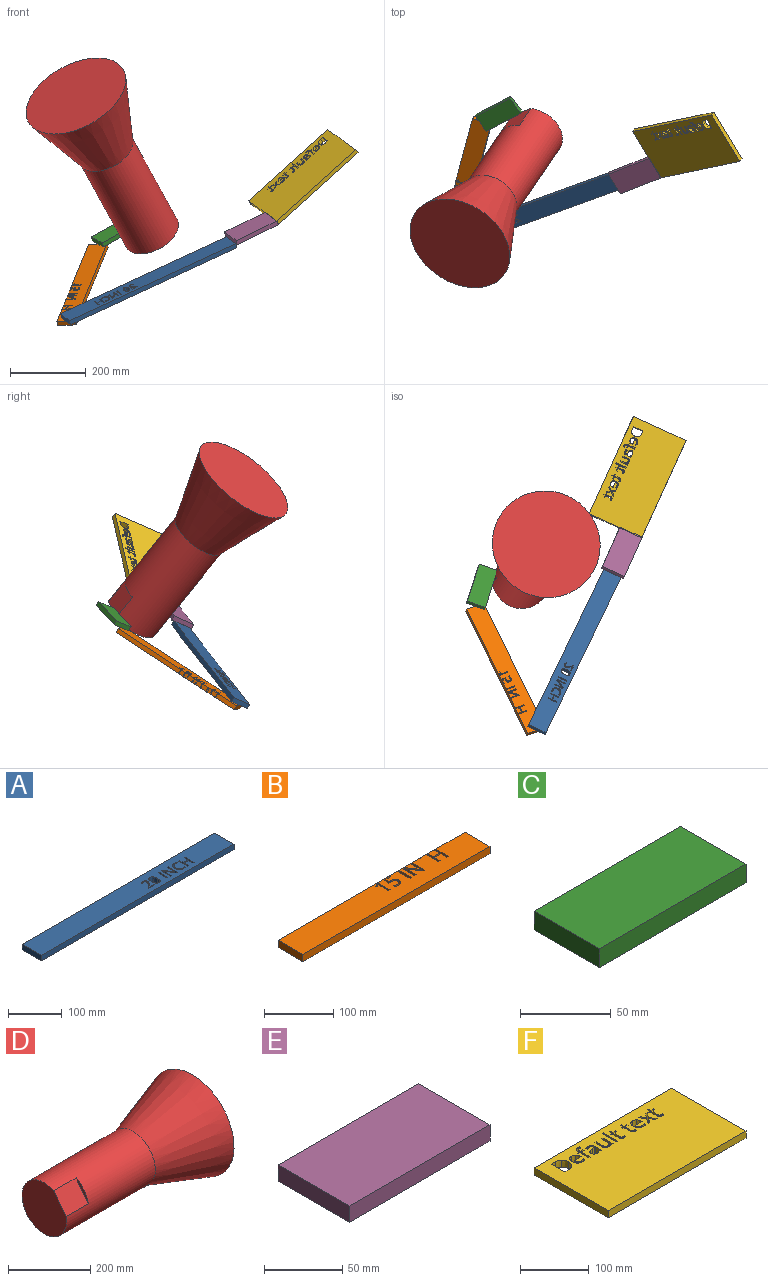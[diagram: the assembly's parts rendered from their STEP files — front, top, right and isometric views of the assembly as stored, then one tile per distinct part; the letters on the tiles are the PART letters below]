
ASSEMBLY  parts=6 mates=5
PART A: 80 faces, bbox 508x50.8x12.7 mm
  f0: plane 12.7x2.44mm, normal (-1,0,0), area 31mm2, adj f1,f77,f78,f79
  f1: plane 15.23x12.7mm, normal (0,1,0), area 193.5mm2, adj f0,f2,f78,f79
  f2: plane 12.7x2.27mm, normal (1,0,0), area 28.8mm2, adj f1,f3,f78,f79
  f3: plane 12.7x6.13mm, normal (0.71,-0.71,0), area 109.9mm2, adj f2,f4,f78,f79
  f4: extruded ~12.7x4.03mm, area 69.3mm2, adj f3,f5,f78,f79
  f5: extruded ~12.7x2.35mm, area 34.4mm2, adj f4,f6,f78,f79
  f6: extruded ~12.7x2.46mm, area 31.9mm2, adj f5,f7,f78,f79
  f7: extruded ~12.7x2.94mm, area 41.2mm2, adj f6,f8,f78,f79
  f8: extruded ~12.7x3.13mm, area 43.1mm2, adj f7,f9,f78,f79
  f9: extruded ~12.7x2.73mm, area 35.4mm2, adj f8,f10,f78,f79
  f10: extruded ~12.7x2.88mm, area 42.8mm2, adj f9,f11,f78,f79
  f11: plane 12.7x1.79mm, normal (0.79,0.61,0), area 28.8mm2, adj f10,f12,f78,f79
  f12: extruded ~12.7x6.98mm, area 96.8mm2, adj f11,f13,f78,f79
  f13: extruded ~12.7x5.12mm, area 70mm2, adj f12,f14,f78,f79
  f14: extruded ~12.7x4.49mm, area 63.7mm2, adj f13,f15,f78,f79
  f15: extruded ~12.7x4.36mm, area 58.3mm2, adj f14,f16,f78,f79
  f16: extruded ~12.7x5.45mm, area 91.1mm2, adj f15,f17,f78,f79
  f17: plane 12.7x5.07mm, normal (-0.7,0.71,0), area 90.1mm2, adj f16,f18,f78,f79
  f18: plane 12.7x0.13mm, normal (-1,0,0), area 1.6mm2, adj f17,f77,f78,f79
  f19: extruded ~12.7x8.86mm, area 116.7mm2, adj f20,f71,f78,f79
  f20: extruded ~12.7x8.98mm, area 118mm2, adj f19,f21,f78,f79
  f21: extruded ~12.7x5.8mm, area 86.6mm2, adj f20,f22,f78,f79
  f22: extruded ~12.7x5.69mm, area 85.8mm2, adj f21,f23,f78,f79
  f23: extruded ~12.7x8.91mm, area 117.3mm2, adj f22,f24,f78,f79
  f24: extruded ~12.7x8.99mm, area 118.1mm2, adj f23,f25,f78,f79
  f25: extruded ~12.7x5.75mm, area 85.9mm2, adj f24,f71,f78,f79
  f26: plane 23.18x12.7mm, normal (-1,0,0), area 294.4mm2, adj f27,f72,f78,f79
  f27: plane 12.7x2.69mm, normal (0,1,0), area 34.2mm2, adj f26,f28,f78,f79
  f28: plane 12.7x10.91mm, normal (1,0,0), area 138.5mm2, adj f27,f29,f78,f79
  f29: plane 12.7x12.21mm, normal (0,1,0), area 155.1mm2, adj f28,f30,f78,f79
  f30: plane 12.7x10.91mm, normal (-1,0,0), area 138.5mm2, adj f29,f31,f78,f79
  f31: plane 12.7x2.69mm, normal (0,1,0), area 34.2mm2, adj f30,f32,f78,f79
  f32: plane 23.18x12.7mm, normal (1,0,0), area 294.4mm2, adj f31,f33,f78,f79
  f33: plane 12.7x2.69mm, normal (0,-1,0), area 34.2mm2, adj f32,f34,f78,f79
  f34: plane 12.7x9.86mm, normal (-1,0,0), area 125.2mm2, adj f33,f35,f78,f79
  f35: plane 12.7x12.21mm, normal (0,-1,0), area 155.1mm2, adj f34,f36,f78,f79
  f36: plane 12.7x9.86mm, normal (1,0,0), area 125.2mm2, adj f35,f72,f78,f79
  f37: extruded ~12.7x5.27mm, area 69.2mm2, adj f38,f73,f78,f79
  f38: extruded ~12.7x6.03mm, area 85.9mm2, adj f37,f39,f78,f79
  f39: extruded ~12.7x6.97mm, area 94.9mm2, adj f38,f40,f78,f79
  f40: extruded ~12.7x7.03mm, area 95.3mm2, adj f39,f41,f78,f79
  f41: extruded ~12.7x6.08mm, area 86.2mm2, adj f40,f42,f78,f79
  f42: extruded ~12.7x5.53mm, area 71.4mm2, adj f41,f43,f78,f79
  f43: plane 12.7x2.36mm, normal (-1,0,0), area 30mm2, adj f42,f44,f78,f79
  f44: extruded ~12.7x5.95mm, area 76.8mm2, adj f43,f45,f78,f79
  f45: extruded ~12.7x7.9mm, area 111.3mm2, adj f44,f46,f78,f79
  f46: extruded ~12.7x8.83mm, area 120.3mm2, adj f45,f47,f78,f79
  f47: extruded ~12.7x6.28mm, area 82.2mm2, adj f46,f48,f78,f79
  f48: extruded ~12.7x4.15mm, area 73.1mm2, adj f47,f49,f78,f79
  f49: extruded ~12.7x5.95mm, area 78.7mm2, adj f48,f50,f78,f79
  f50: extruded ~12.7x6.37mm, area 83.4mm2, adj f49,f73,f78,f79
  f51: plane 23.18x12.7mm, normal (-1,0,0), area 294.4mm2, adj f52,f74,f78,f79
  f52: plane 12.7x3.07mm, normal (0,1,0), area 39mm2, adj f51,f53,f78,f79
  f53: plane 19.45x12.7mm, normal (0.84,0.55,0), area 294.8mm2, adj f52,f54,f78,f79
  f54: plane 12.7x0.13mm, normal (0,1,0), area 1.6mm2, adj f53,f55,f78,f79
  f55: extruded ~12.7x6.28mm, area 79.8mm2, adj f54,f56,f78,f79
  f56: plane 13.17x12.7mm, normal (-1,0,0), area 167.3mm2, adj f55,f57,f78,f79
  f57: plane 12.7x2.49mm, normal (0,1,0), area 31.6mm2, adj f56,f58,f78,f79
  f58: plane 23.18x12.7mm, normal (1,0,0), area 294.4mm2, adj f57,f59,f78,f79
  f59: plane 12.7x3.04mm, normal (0,-1,0), area 38.7mm2, adj f58,f60,f78,f79
  f60: plane 19.37x12.7mm, normal (-0.84,-0.55,0), area 293.8mm2, adj f59,f61,f78,f79
  f61: plane 12.7x0.13mm, normal (0,-1,0), area 1.6mm2, adj f60,f62,f78,f79
  f62: extruded ~12.7x2.75mm, area 35mm2, adj f61,f63,f78,f79
  f63: extruded ~12.7x3.32mm, area 42.2mm2, adj f62,f64,f78,f79
  f64: plane 13.3x12.7mm, normal (1,0,0), area 168.9mm2, adj f63,f74,f78,f79
  f65: plane 12.7x2.69mm, normal (0,1,0), area 34.2mm2, adj f66,f75,f78,f79
  f66: plane 23.18x12.7mm, normal (1,0,0), area 294.4mm2, adj f65,f67,f78,f79
  f67: plane 12.7x2.69mm, normal (0,-1,0), area 34.2mm2, adj f66,f75,f78,f79
  f68: plane 50.8x12.7mm, normal (1,0,0), area 645.2mm2, adj f69,f76,f78,f79
  f69: plane 508x12.7mm, normal (0,1,0), area 6451.6mm2, adj f68,f70,f78,f79
  f70: plane 50.8x12.7mm, normal (-1,0,0), area 645.2mm2, adj f69,f76,f78,f79
  f71: extruded ~12.7x5.73mm, area 86.5mm2, adj f19,f25,f78,f79
  f72: plane 12.7x2.69mm, normal (0,-1,0), area 34.2mm2, adj f26,f36,f78,f79
  f73: plane 12.7x2.31mm, normal (-0.9,0.44,0), area 32.8mm2, adj f37,f50,f78,f79
  f74: plane 12.7x2.52mm, normal (0,-1,0), area 32mm2, adj f51,f64,f78,f79
  f75: plane 23.18x12.7mm, normal (-1,0,0), area 294.4mm2, adj f65,f67,f78,f79
  f76: plane 508x12.7mm, normal (0,-1,0), area 6451.6mm2, adj f68,f70,f78,f79
  f77: plane 12.7x11.92mm, normal (0,-1,0), area 151.4mm2, adj f0,f18,f78,f79
  f78: plane 508x50.8mm, normal (0,0,1), area 24872.1mm2, adj f0,f1,f2,f3,f4,f5,f6,f7
  f79: plane 508x50.8mm, normal (0,0,-1), area 24872.1mm2, adj f0,f1,f2,f3,f4,f5,f6,f7
PART B: 68 faces, bbox 381x50.9x12.7 mm
  f0: plane 25.19x12.7mm, normal (-1,0,0), area 319.8mm2, adj f1,f65,f66,f67
  f1: plane 12.7x2.79mm, normal (0,1,0), area 35.4mm2, adj f0,f2,f66,f67
  f2: plane 17.95x12.7mm, normal (1,0,0), area 227.9mm2, adj f1,f3,f66,f67
  f3: extruded ~12.7x4.24mm, area 53.9mm2, adj f2,f4,f66,f67
  f4: extruded ~12.7x0.81mm, area 14.1mm2, adj f3,f5,f66,f67
  f5: extruded ~12.7x4.1mm, area 67.3mm2, adj f4,f6,f66,f67
  f6: plane 12.7x1.96mm, normal (0.79,0.61,0), area 31.5mm2, adj f5,f7,f66,f67
  f7: plane 12.7x6.66mm, normal (0.61,-0.79,0), area 107mm2, adj f6,f65,f66,f67
  f8: extruded ~12.7x3.95mm, area 50.5mm2, adj f9,f60,f66,f67
  f9: extruded ~12.7x6.26mm, area 85.2mm2, adj f8,f10,f66,f67
  f10: extruded ~12.7x5.4mm, area 77mm2, adj f9,f11,f66,f67
  f11: extruded ~12.7x6.13mm, area 86.7mm2, adj f10,f12,f66,f67
  f12: extruded ~12.7x6.87mm, area 93.8mm2, adj f11,f13,f66,f67
  f13: extruded ~12.7x6.49mm, area 85.3mm2, adj f12,f14,f66,f67
  f14: plane 12.7x2.76mm, normal (1,0,0), area 35mm2, adj f13,f15,f66,f67
  f15: extruded ~12.7x2.99mm, area 41.2mm2, adj f14,f16,f66,f67
  f16: extruded ~12.7x3.53mm, area 45.3mm2, adj f15,f17,f66,f67
  f17: extruded ~12.7x4.71mm, area 63.8mm2, adj f16,f18,f66,f67
  f18: extruded ~12.7x4.14mm, area 58.6mm2, adj f17,f19,f66,f67
  f19: extruded ~12.7x6.45mm, area 121.1mm2, adj f18,f20,f66,f67
  f20: extruded ~12.7x4.38mm, area 56mm2, adj f19,f21,f66,f67
  f21: plane 12.7x1.48mm, normal (0.54,0.84,0), area 22.4mm2, adj f20,f22,f66,f67
  f22: plane 12.7x11.79mm, normal (1,-0.08,0), area 150.2mm2, adj f21,f23,f66,f67
  f23: plane 12.7x12.52mm, normal (0,-1,0), area 159mm2, adj f22,f24,f66,f67
  f24: plane 12.7x2.64mm, normal (-1,0,0), area 33.5mm2, adj f23,f25,f66,f67
  f25: plane 12.7x10.08mm, normal (0,1,0), area 128mm2, adj f24,f60,f66,f67
  f26: plane 12.7x2.93mm, normal (0,1,0), area 37.2mm2, adj f27,f61,f66,f67
  f27: plane 25.19x12.7mm, normal (1,0,0), area 319.8mm2, adj f26,f28,f66,f67
  f28: plane 12.7x2.93mm, normal (0,-1,0), area 37.2mm2, adj f27,f61,f66,f67
  f29: plane 25.19x12.7mm, normal (-1,0,0), area 319.8mm2, adj f30,f62,f66,f67
  f30: plane 12.7x3.34mm, normal (0,1,0), area 42.4mm2, adj f29,f31,f66,f67
  f31: plane 21.13x13.76mm, normal (0.84,0.55,0), area 320.3mm2, adj f30,f32,f66,f67
  f32: plane 12.7x0.14mm, normal (0,1,0), area 1.8mm2, adj f31,f33,f66,f67
  f33: extruded ~12.7x6.82mm, area 86.7mm2, adj f32,f34,f66,f67
  f34: plane 14.32x12.7mm, normal (-1,0,0), area 181.8mm2, adj f33,f35,f66,f67
  f35: plane 12.7x2.71mm, normal (0,1,0), area 34.4mm2, adj f34,f36,f66,f67
  f36: plane 25.19x12.7mm, normal (1,0,0), area 319.8mm2, adj f35,f37,f66,f67
  f37: plane 12.7x3.31mm, normal (0,-1,0), area 42mm2, adj f36,f38,f66,f67
  f38: plane 21.05x13.73mm, normal (-0.84,-0.55,0), area 319.2mm2, adj f37,f39,f66,f67
  f39: plane 12.7x0.14mm, normal (0,-1,0), area 1.8mm2, adj f38,f40,f66,f67
  f40: extruded ~12.7x2.99mm, area 38mm2, adj f39,f41,f66,f67
  f41: extruded ~12.7x3.61mm, area 45.9mm2, adj f40,f42,f66,f67
  f42: plane 14.45x12.7mm, normal (1,0,0), area 183.6mm2, adj f41,f62,f66,f67
  f43: plane 25.19x12.7mm, normal (-1,0,0), area 319.8mm2, adj f44,f63,f66,f67
  f44: plane 12.7x2.93mm, normal (0,1,0), area 37.2mm2, adj f43,f45,f66,f67
  f45: plane 12.7x11.85mm, normal (1,0,0), area 150.5mm2, adj f44,f46,f66,f67
  f46: plane 13.27x12.7mm, normal (0,1,0), area 168.5mm2, adj f45,f47,f66,f67
  f47: plane 12.7x11.85mm, normal (-1,0,0), area 150.5mm2, adj f46,f48,f66,f67
  f48: plane 12.7x2.93mm, normal (0,1,0), area 37.2mm2, adj f47,f49,f66,f67
  f49: plane 25.19x12.7mm, normal (1,0,0), area 319.8mm2, adj f48,f50,f66,f67
  f50: plane 12.7x2.93mm, normal (0,-1,0), area 37.2mm2, adj f49,f51,f66,f67
  f51: plane 12.7x10.72mm, normal (-1,0,0), area 136.1mm2, adj f50,f52,f66,f67
  f52: plane 13.27x12.7mm, normal (0,-1,0), area 168.5mm2, adj f51,f53,f66,f67
  f53: plane 12.7x10.72mm, normal (1,0,0), area 136.1mm2, adj f52,f63,f66,f67
  f54: extruded ~12.7x2.15mm, area 27.4mm2, adj f55,f64,f66,f67
  f55: plane 288.57x12.7mm, normal (0,1,0), area 3664.8mm2, adj f54,f56,f66,f67
  f56: plane 50.8x12.7mm, normal (-1,0,0), area 645.2mm2, adj f55,f57,f66,f67
  f57: plane 381x12.7mm, normal (0,-1,0), area 4838.7mm2, adj f56,f58,f66,f67
  f58: plane 50.8x12.7mm, normal (1,0,0), area 645.2mm2, adj f57,f59,f66,f67
  f59: plane 87.89x12.7mm, normal (0,1,0), area 1116.2mm2, adj f58,f64,f66,f67
  f60: plane 12.7x7.56mm, normal (-1,0.08,0), area 96.4mm2, adj f8,f25,f66,f67
  f61: plane 25.19x12.7mm, normal (-1,0,0), area 319.8mm2, adj f26,f28,f66,f67
  f62: plane 12.7x2.74mm, normal (0,-1,0), area 34.8mm2, adj f29,f42,f66,f67
  f63: plane 12.7x2.93mm, normal (0,-1,0), area 37.2mm2, adj f43,f53,f66,f67
  f64: extruded ~12.7x2.4mm, area 30.5mm2, adj f54,f59,f66,f67
  f65: plane 12.7x2.41mm, normal (0,-1,0), area 30.6mm2, adj f0,f7,f66,f67
  f66: plane 381x50.94mm, normal (0,0,1), area 18655.9mm2, adj f0,f1,f2,f3,f4,f5,f6,f7
  f67: plane 381x50.94mm, normal (0,0,-1), area 18655.9mm2, adj f0,f1,f2,f3,f4,f5,f6,f7
PART C: 6 faces, bbox 114.3x50.8x12.7 mm
  f0: plane 50.8x12.7mm, normal (1,0,0), area 645.2mm2, adj f1,f3,f4,f5
  f1: plane 114.3x12.7mm, normal (0,1,0), area 1451.6mm2, adj f0,f2,f4,f5
  f2: plane 50.8x12.7mm, normal (-1,0,0), area 645.2mm2, adj f1,f3,f4,f5
  f3: plane 114.3x12.7mm, normal (0,-1,0), area 1451.6mm2, adj f0,f2,f4,f5
  f4: plane 114.3x50.8mm, normal (0,0,1), area 5806.4mm2, adj f0,f1,f2,f3
  f5: plane 114.3x50.8mm, normal (0,0,-1), area 5806.4mm2, adj f0,f1,f2,f3
PART D: 6 faces, bbox 508x286.1x286.1 mm
  f0: cylinder r=76.2mm len=304.8mm, axis (-1,0,0), area 140438.7mm2, adj f1,f3,f4,f5
  f1: plane 152.4x152.4mm, normal (-1,0,0), area 17849.7mm2, adj f0,f4
  f2: plane 286.07x286.07mm, normal (1,0,0), area 64273.6mm2, adj f3
  f3: cone r=76.2mm half-angle=18.2deg, axis (1,0,0), area 147329.1mm2, adj f0,f2
  f4: plane 76.2x55.25mm, normal (0,-0.8,0.61), area 5290.5mm2, adj f0,f1,f5
  f5: plane 55.25x42.05mm, normal (-1,0,0), area 391.7mm2, adj f0,f4
PART E: 6 faces, bbox 127x64.3x12.7 mm
  f0: plane 127x12.7mm, normal (0,-1,0), area 1612.9mm2, adj f1,f3,f4,f5
  f1: plane 64.28x12.7mm, normal (1,0,0), area 816.4mm2, adj f0,f2,f4,f5
  f2: plane 127x12.7mm, normal (0,1,0), area 1612.9mm2, adj f1,f3,f4,f5
  f3: plane 64.28x12.7mm, normal (-1,0,0), area 816.4mm2, adj f0,f2,f4,f5
  f4: plane 127x64.28mm, normal (0,0,1), area 8164.1mm2, adj f0,f1,f2,f3
  f5: plane 127x64.28mm, normal (0,0,-1), area 8164.1mm2, adj f0,f1,f2,f3
PART F: 167 faces, bbox 284.2x152.4x12.7 mm
  f0: plane 284.16x152.4mm, normal (0,0,1), area 41292.7mm2, adj f2,f3,f4,f5,f6,f7,f8,f9
  f1: plane 284.16x152.4mm, normal (0,0,-1), area 41292.7mm2, adj f2,f3,f4,f5,f6,f7,f8,f9
  f2: plane 284.16x12.7mm, normal (0,-1,0), area 3608.9mm2, adj f0,f1,f3,f5
  f3: plane 152.4x12.7mm, normal (1,0,0), area 1935.5mm2, adj f0,f1,f2,f4
  f4: plane 284.16x12.7mm, normal (0,1,0), area 3608.9mm2, adj f0,f1,f3,f5
  f5: plane 152.4x12.7mm, normal (-1,0,0), area 1935.5mm2, adj f0,f1,f2,f4
  f6: plane 12.7x5.21mm, normal (0,1,0), area 66.1mm2, adj f0,f1,f7,f22
  f7: plane 12.7x2.41mm, normal (-1,0,0), area 30.6mm2, adj f0,f1,f6,f8
  f8: plane 12.7x5.21mm, normal (0,-1,0), area 66.1mm2, adj f0,f1,f7,f9
  f9: plane 12.7x1.33mm, normal (-1,0,0), area 16.8mm2, adj f0,f1,f8,f10
  f10: extruded ~12.7x3.74mm, area 49.4mm2, adj f0,f1,f9,f11
  f11: extruded ~12.7x2.59mm, area 37.6mm2, adj f0,f1,f10,f12
  f12: extruded ~12.7x3.06mm, area 39.7mm2, adj f0,f1,f11,f13
  f13: plane 12.7x2.48mm, normal (-0.95,0.31,0), area 33.2mm2, adj f0,f1,f12,f14
  f14: extruded ~12.7x3.81mm, area 49.2mm2, adj f0,f1,f13,f15
  f15: extruded ~12.7x7.54mm, area 145.7mm2, adj f0,f1,f14,f16
  f16: plane 12.7x1.13mm, normal (1,0,0), area 14.4mm2, adj f0,f1,f15,f17
  f17: plane 12.7x3.65mm, normal (0.29,-0.96,0), area 48.5mm2, adj f0,f1,f16,f18
  f18: plane 12.7x1.4mm, normal (1,0,0), area 17.7mm2, adj f0,f1,f17,f19
  f19: plane 12.7x3.65mm, normal (0,1,0), area 46.4mm2, adj f0,f1,f18,f20
  f20: plane 18.04x12.7mm, normal (1,0,0), area 229.1mm2, adj f0,f1,f19,f21
  f21: plane 12.7x3.1mm, normal (0,1,0), area 39.3mm2, adj f0,f1,f20,f22
  f22: plane 18.04x12.7mm, normal (-1,0,0), area 229.1mm2, adj f0,f1,f6,f21
  f23: extruded ~12.7x7.15mm, area 100.3mm2, adj f0,f1,f24,f36
  f24: extruded ~12.7x3.53mm, area 45.1mm2, adj f0,f1,f23,f25
  f25: extruded ~12.7x3.1mm, area 41.5mm2, adj f0,f1,f24,f26
  f26: plane 12.7x2.76mm, normal (-1,0,0), area 35.1mm2, adj f0,f1,f25,f27
  f27: extruded ~12.7x6.52mm, area 85.3mm2, adj f0,f1,f26,f28
  f28: extruded ~12.7x4.86mm, area 68.1mm2, adj f0,f1,f27,f29
  f29: extruded ~12.7x5.47mm, area 74.8mm2, adj f0,f1,f28,f30
  f30: plane 14.08x12.7mm, normal (0,1,0), area 178.8mm2, adj f0,f1,f29,f31
  f31: plane 12.7x1.96mm, normal (-1,0,0), area 24.9mm2, adj f0,f1,f30,f32
  f32: extruded ~12.7x6.67mm, area 91.4mm2, adj f0,f1,f31,f33
  f33: extruded ~12.7x6.08mm, area 86.3mm2, adj f0,f1,f32,f34
  f34: extruded ~12.7x6.54mm, area 94.1mm2, adj f0,f1,f33,f35
  f35: extruded ~12.7x7.86mm, area 106.7mm2, adj f0,f1,f34,f36
  f36: extruded ~12.7x7.67mm, area 105.5mm2, adj f0,f1,f23,f35
  f37: plane 12.7x2.91mm, normal (0.98,0.21,0), area 37.8mm2, adj f0,f1,f38,f55
  f38: plane 12.7x2.3mm, normal (0,1,0), area 29.2mm2, adj f0,f1,f37,f39
  f39: plane 13.96x12.7mm, normal (-1,0,0), area 177.3mm2, adj f0,f1,f38,f40
  f40: extruded ~12.7x5.2mm, area 71.8mm2, adj f0,f1,f39,f41
  f41: extruded ~12.7x5.42mm, area 73.5mm2, adj f0,f1,f40,f42
  f42: extruded ~12.7x3.61mm, area 46.4mm2, adj f0,f1,f41,f43
  f43: extruded ~12.7x3.31mm, area 45.2mm2, adj f0,f1,f42,f44
  f44: plane 12.7x2.37mm, normal (0.93,0.37,0), area 32.5mm2, adj f0,f1,f43,f45
  f45: extruded ~12.7x5.78mm, area 76.7mm2, adj f0,f1,f44,f46
  f46: extruded ~12.7x3.31mm, area 45.9mm2, adj f0,f1,f45,f47
  f47: extruded ~12.7x3.55mm, area 48mm2, adj f0,f1,f46,f48
  f48: plane 12.7x1.27mm, normal (1,0,0), area 16.1mm2, adj f0,f1,f47,f49
  f49: plane 12.7x3.47mm, normal (0.03,-1,0), area 44.1mm2, adj f0,f1,f48,f50
  f50: extruded ~12.7x9.9mm, area 169mm2, adj f0,f1,f49,f51
  f51: extruded ~12.7x4.46mm, area 62.6mm2, adj f0,f1,f50,f52
  f52: extruded ~12.7x4.76mm, area 65.2mm2, adj f0,f1,f51,f53
  f53: extruded ~12.7x3.8mm, area 49.4mm2, adj f0,f1,f52,f54
  f54: extruded ~12.7x3.05mm, area 51.4mm2, adj f0,f1,f53,f55
  f55: plane 12.7x0.15mm, normal (0,1,0), area 1.9mm2, adj f0,f1,f37,f54
  f56: plane 13.26x12.7mm, normal (-1,0,0), area 168.5mm2, adj f0,f1,f57,f72
  f57: plane 12.7x3.13mm, normal (0,-1,0), area 39.8mm2, adj f0,f1,f56,f58
  f58: plane 13.38x12.7mm, normal (1,0,0), area 169.9mm2, adj f0,f1,f57,f59
  f59: extruded ~12.7x5.67mm, area 77.9mm2, adj f0,f1,f58,f60
  f60: extruded ~12.7x5.58mm, area 76.3mm2, adj f0,f1,f59,f61
  f61: extruded ~12.7x3.86mm, area 50.4mm2, adj f0,f1,f60,f62
  f62: extruded ~12.7x2.64mm, area 45.2mm2, adj f0,f1,f61,f63
  f63: plane 12.7x0.17mm, normal (0,1,0), area 2.1mm2, adj f0,f1,f62,f64
  f64: plane 12.7x2.74mm, normal (0.99,0.16,0), area 35.3mm2, adj f0,f1,f63,f65
  f65: plane 12.7x2.56mm, normal (0,1,0), area 32.4mm2, adj f0,f1,f64,f66
  f66: plane 20.45x12.7mm, normal (-1,0,0), area 259.7mm2, adj f0,f1,f65,f67
  f67: plane 12.7x3.1mm, normal (0,-1,0), area 39.3mm2, adj f0,f1,f66,f68
  f68: plane 12.7x10.75mm, normal (1,0,0), area 136.5mm2, adj f0,f1,f67,f69
  f69: extruded ~12.7x5.73mm, area 76.6mm2, adj f0,f1,f68,f70
  f70: extruded ~12.7x4.69mm, area 65.7mm2, adj f0,f1,f69,f71
  f71: extruded ~12.7x3.56mm, area 49.2mm2, adj f0,f1,f70,f72
  f72: extruded ~12.7x3.73mm, area 50.7mm2, adj f0,f1,f56,f71
  f73: plane 12.7x3.1mm, normal (0,1,0), area 39.3mm2, adj f0,f1,f74,f76
  f74: plane 29.03x12.7mm, normal (-1,0,0), area 368.7mm2, adj f0,f1,f73,f75
  f75: plane 12.7x3.1mm, normal (0,-1,0), area 39.3mm2, adj f0,f1,f74,f76
  f76: plane 29.03x12.7mm, normal (1,0,0), area 368.7mm2, adj f0,f1,f73,f75
  f77: extruded ~12.7x1.59mm, area 20.2mm2, adj f0,f1,f78,f95
  f78: extruded ~12.7x2.41mm, area 34.1mm2, adj f0,f1,f77,f79
  f79: extruded ~12.7x2.83mm, area 38.5mm2, adj f0,f1,f78,f80
  f80: plane 12.7x12.03mm, normal (-1,0,0), area 152.8mm2, adj f0,f1,f79,f81
  f81: plane 12.7x5.93mm, normal (0,1,0), area 75.4mm2, adj f0,f1,f80,f82
  f82: plane 12.7x2.41mm, normal (-1,0,0), area 30.6mm2, adj f0,f1,f81,f83
  f83: plane 12.7x5.93mm, normal (0,-1,0), area 75.4mm2, adj f0,f1,f82,f84
  f84: plane 12.7x4.74mm, normal (-1,0,0), area 60.2mm2, adj f0,f1,f83,f85
  f85: plane 12.7x1.79mm, normal (0,-1,0), area 22.7mm2, adj f0,f1,f84,f86
  f86: plane 12.7x4.36mm, normal (0.96,-0.29,0), area 57.8mm2, adj f0,f1,f85,f87
  f87: plane 12.7x2.93mm, normal (0.4,-0.92,0), area 40.7mm2, adj f0,f1,f86,f88
  f88: plane 12.7x1.49mm, normal (1,0,0), area 19mm2, adj f0,f1,f87,f89
  f89: plane 12.7x2.93mm, normal (0,1,0), area 37.2mm2, adj f0,f1,f88,f90
  f90: plane 12.7x12.17mm, normal (1,0,0), area 154.5mm2, adj f0,f1,f89,f91
  f91: extruded ~12.7x6.25mm, area 125.5mm2, adj f0,f1,f90,f92
  f92: extruded ~12.7x1.77mm, area 22.6mm2, adj f0,f1,f91,f93
  f93: extruded ~12.7x1.48mm, area 19.5mm2, adj f0,f1,f92,f94
  f94: plane 12.7x2.37mm, normal (-1,0,0), area 30.1mm2, adj f0,f1,f93,f95
  f95: extruded ~12.7x1.21mm, area 15.7mm2, adj f0,f1,f77,f94
  f96: extruded ~12.7x1.59mm, area 20.2mm2, adj f0,f1,f97,f114
  f97: extruded ~12.7x2.41mm, area 34.1mm2, adj f0,f1,f96,f98
  f98: extruded ~12.7x2.83mm, area 38.5mm2, adj f0,f1,f97,f99
  f99: plane 12.7x12.03mm, normal (-1,0,0), area 152.8mm2, adj f0,f1,f98,f100
  f100: plane 12.7x5.93mm, normal (0,1,0), area 75.4mm2, adj f0,f1,f99,f101
  f101: plane 12.7x2.41mm, normal (-1,0,0), area 30.6mm2, adj f0,f1,f100,f102
  f102: plane 12.7x5.93mm, normal (0,-1,0), area 75.4mm2, adj f0,f1,f101,f103
  f103: plane 12.7x4.74mm, normal (-1,0,0), area 60.2mm2, adj f0,f1,f102,f104
  f104: plane 12.7x1.79mm, normal (0,-1,0), area 22.7mm2, adj f0,f1,f103,f105
  f105: plane 12.7x4.36mm, normal (0.96,-0.29,0), area 57.8mm2, adj f0,f1,f104,f106
  f106: plane 12.7x2.93mm, normal (0.4,-0.92,0), area 40.7mm2, adj f0,f1,f105,f107
  f107: plane 12.7x1.49mm, normal (1,0,0), area 19mm2, adj f0,f1,f106,f108
  f108: plane 12.7x2.93mm, normal (0,1,0), area 37.2mm2, adj f0,f1,f107,f109
  f109: plane 12.7x12.17mm, normal (1,0,0), area 154.5mm2, adj f0,f1,f108,f110
  f110: extruded ~12.7x6.25mm, area 125.5mm2, adj f0,f1,f109,f111
  f111: extruded ~12.7x1.77mm, area 22.6mm2, adj f0,f1,f110,f112
  f112: extruded ~12.7x1.48mm, area 19.5mm2, adj f0,f1,f111,f113
  f113: plane 12.7x2.37mm, normal (-1,0,0), area 30.1mm2, adj f0,f1,f112,f114
  f114: extruded ~12.7x1.21mm, area 15.7mm2, adj f0,f1,f96,f113
  f115: plane 12.7x9.98mm, normal (0.81,0.58,0), area 155.6mm2, adj f0,f1,f116,f126
  f116: plane 12.7x10.46mm, normal (0.81,-0.58,0), area 163.4mm2, adj f0,f1,f115,f117
  f117: plane 12.7x3.5mm, normal (0,1,0), area 44.5mm2, adj f0,f1,f116,f118
  f118: plane 12.7x8.29mm, normal (-0.82,0.57,0), area 128.3mm2, adj f0,f1,f117,f119
  f119: plane 12.7x8.29mm, normal (0.82,0.57,0), area 127.9mm2, adj f0,f1,f118,f120
  f120: plane 12.7x3.5mm, normal (0,1,0), area 44.5mm2, adj f0,f1,f119,f121
  f121: plane 12.7x10.46mm, normal (-0.81,-0.58,0), area 163.4mm2, adj f0,f1,f120,f122
  f122: plane 12.7x9.98mm, normal (-0.81,0.58,0), area 155.6mm2, adj f0,f1,f121,f123
  f123: plane 12.7x3.49mm, normal (0,-1,0), area 44.4mm2, adj f0,f1,f122,f124
  f124: plane 12.7x7.83mm, normal (0.82,-0.57,0), area 120.6mm2, adj f0,f1,f123,f125
  f125: plane 12.7x7.83mm, normal (-0.82,-0.57,0), area 120.8mm2, adj f0,f1,f124,f126
  f126: plane 12.7x3.53mm, normal (0,-1,0), area 44.8mm2, adj f0,f1,f115,f125
  f127: extruded ~12.7x1.59mm, area 20.2mm2, adj f0,f1,f128,f145
  f128: extruded ~12.7x2.41mm, area 34.1mm2, adj f0,f1,f127,f129
  f129: extruded ~12.7x2.83mm, area 38.5mm2, adj f0,f1,f128,f130
  f130: plane 12.7x12.03mm, normal (-1,0,0), area 152.8mm2, adj f0,f1,f129,f131
  f131: plane 12.7x5.93mm, normal (0,1,0), area 75.4mm2, adj f0,f1,f130,f132
  f132: plane 12.7x2.41mm, normal (-1,0,0), area 30.6mm2, adj f0,f1,f131,f133
  f133: plane 12.7x5.93mm, normal (0,-1,0), area 75.4mm2, adj f0,f1,f132,f134
  f134: plane 12.7x4.74mm, normal (-1,0,0), area 60.2mm2, adj f0,f1,f133,f135
  f135: plane 12.7x1.79mm, normal (0,-1,0), area 22.7mm2, adj f0,f1,f134,f136
  f136: plane 12.7x4.36mm, normal (0.96,-0.29,0), area 57.8mm2, adj f0,f1,f135,f137
  f137: plane 12.7x2.93mm, normal (0.4,-0.92,0), area 40.7mm2, adj f0,f1,f136,f138
  f138: plane 12.7x1.49mm, normal (1,0,0), area 19mm2, adj f0,f1,f137,f139
  f139: plane 12.7x2.93mm, normal (0,1,0), area 37.2mm2, adj f0,f1,f138,f140
  f140: plane 12.7x12.17mm, normal (1,0,0), area 154.5mm2, adj f0,f1,f139,f141
  f141: extruded ~12.7x6.25mm, area 125.5mm2, adj f0,f1,f140,f142
  f142: extruded ~12.7x1.77mm, area 22.6mm2, adj f0,f1,f141,f143
  f143: extruded ~12.7x1.48mm, area 19.5mm2, adj f0,f1,f142,f144
  f144: plane 12.7x2.37mm, normal (-1,0,0), area 30.1mm2, adj f0,f1,f143,f145
  f145: extruded ~12.7x1.21mm, area 15.7mm2, adj f0,f1,f127,f144
  f146: extruded ~12.7x10.32mm, area 143mm2, adj f0,f1,f147,f152
  f147: extruded ~12.7x9.85mm, area 136.5mm2, adj f0,f1,f146,f148
  f148: extruded ~12.7x9.89mm, area 137mm2, adj f0,f1,f147,f149
  f149: plane 12.7x8.36mm, normal (0,-1,0), area 106.1mm2, adj f0,f1,f148,f150
  f150: plane 27.28x12.7mm, normal (1,0,0), area 346.4mm2, adj f0,f1,f149,f151
  f151: plane 12.7x7.56mm, normal (0,1,0), area 96mm2, adj f0,f1,f150,f152
  f152: extruded ~12.7x10.55mm, area 145.1mm2, adj f0,f1,f146,f151
  f153: extruded ~12.7x7.15mm, area 100.3mm2, adj f0,f1,f154,f166
  f154: extruded ~12.7x3.53mm, area 45.1mm2, adj f0,f1,f153,f155
  f155: extruded ~12.7x3.1mm, area 41.5mm2, adj f0,f1,f154,f156
  f156: plane 12.7x2.76mm, normal (-1,0,0), area 35.1mm2, adj f0,f1,f155,f157
  f157: extruded ~12.7x6.52mm, area 85.3mm2, adj f0,f1,f156,f158
  f158: extruded ~12.7x4.86mm, area 68.1mm2, adj f0,f1,f157,f159
  f159: extruded ~12.7x5.47mm, area 74.8mm2, adj f0,f1,f158,f160
  f160: plane 14.08x12.7mm, normal (0,1,0), area 178.8mm2, adj f0,f1,f159,f161
  f161: plane 12.7x1.96mm, normal (-1,0,0), area 24.9mm2, adj f0,f1,f160,f162
  f162: extruded ~12.7x6.67mm, area 91.4mm2, adj f0,f1,f161,f163
  f163: extruded ~12.7x6.08mm, area 86.3mm2, adj f0,f1,f162,f164
  f164: extruded ~12.7x6.54mm, area 94.1mm2, adj f0,f1,f163,f165
  f165: extruded ~12.7x7.86mm, area 106.7mm2, adj f0,f1,f164,f166
  f166: extruded ~12.7x7.67mm, area 105.5mm2, adj f0,f1,f153,f165
PLACE A rot(axis=(-0.21,0.95,0.23),161.3deg) t=(3390.19,1092.73,-1540.57)mm
PLACE B rot(axis=(-0.59,0.79,0.15),151.9deg) t=(3681.32,700.7,-1713.36)mm
PLACE C rot(axis=(0.57,-0.46,0.69),45.3deg) t=(4127.64,1202.14,-1307.23)mm
PLACE D rot(axis=(-0.34,-0.29,-0.9),124.9deg) t=(3487.54,670.57,282.21)mm
PLACE E rot(axis=(-0.22,0.95,0.23),161deg) t=(4442.94,1572.59,-980.66)mm
PLACE F rot(axis=(-0.19,0.94,0.27),142.8deg) t=(4377.01,1738.82,-868.34)mm
MATE revolute F.f2 <-> E.f0  axis (0.48,-0.8,-0.35) through (4375.8,1638.81,-966.04)mm
MATE revolute B.f67 <-> A.f78  axis (-0.21,-0.5,0.84) through (3818.31,1473.07,-1225.23)mm
MATE revolute C.f5 <-> B.f67  axis (0.21,0.5,-0.84) through (3902.08,1783.99,-1021.58)mm
MATE revolute D.f4 <-> C.f3  axis (-0.56,0.77,0.31) through (4006.29,1808.4,-973.68)mm
MATE revolute A.f79 <-> E.f4  axis (-0.21,-0.5,0.84) through (4253.69,1625.36,-1011.97)mm
